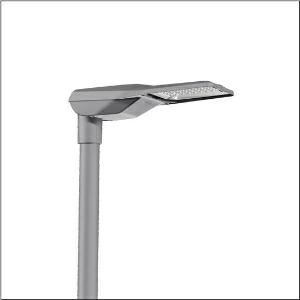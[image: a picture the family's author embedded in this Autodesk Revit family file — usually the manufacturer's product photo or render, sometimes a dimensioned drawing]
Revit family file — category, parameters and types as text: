
# Revit family: streetlight_sl_21_iq_mini___st0_8a_5xe2c31g08gb_0650
name_source: partatom
category: Lighting Fixtures
units: mm (PartAtom-declared; Revit-internal decimal feet)

## family parameters
Cut with Voids When Loaded = No
Host = Face
Light Source = No
Part Type = Normal
Room Calculation Point = No
Round Connector Dimension = Use Diameter
Shared = No

## types (1)
- --- (1 x LED, 5680 lm, 37.1 W, 3000K)
    Apparent Load = 37 VA
    CIE Flux Codes = 38 75 97 100 100
    Color Rendering = 70
    Color Temperature = 3000K
    Default Elevation = 1800 mm
    Description = Streetlight SL 21 iQ mini, mast luminaire, primary light control with lens, of PMMA, primary optical cover: cover, of toughened safety glass, transparent, light distribution: ST0.8a, light emission: direct distribution, primary light characteristic: asymmetric, installation type: post-top, side-entry, LED, High Power LED, rated luminous flux: 5.680lm, luminous efficacy: 153lm/W, light colour: 730, colour temperature: 3000K, control: Street-Remote, Auto-Match, Temp-Guard, Lumen-Switch, Night-Set, Smart-Wire, Light-Fading, Desk-Remote (wireless, voltage-free reading and setting of iQ features in the workshop via application-optimized NFC function/RFID function), optimised constant luminous flux control (CLO 2.0), presetting dimming linear, mains connection: 220..240V, AC, 50/60Hz, start of lifetime: 37W, end of service life: 39W, reduction: 18W, luminaire housing, of diecast aluminium, powder-coated, Siteco® metallic grey (DB 702S), corrosivity category C5 mid according to DIN EN ISO 12944, please order mast flange separately, inclination adjustable: 0°, 5°, 10°, 15°, sealing non-destructively replaceable, multi-level sealing system, length: 628mm, width: 235mm, height: 110mm, mast flange for spigot size: 42mm (side-entry): 5XC10008XM4, 60/48mm (side-entry/post-top): 5XC10108XM2, 76/60mm (side-entry/post-top): 5XC10108XM1, protection rating (complete): IP66, insulation class (complete): insulation class II (safety insulation), certification: CE, ENEC, ENEC+, VDE, impact resistance: IK09, permissible operating ambient temperature for outdoor applications: -40..+50°C, standard-compliant lighting for roads and squares, packaging unit: 1 piece

Light Distribution: ST0.8a
    Height = 110 mm
    Lamp = 1 x LED
    Lamp Light Flux = 5680 lm
    Lamp Power = 37.1 W
    Lamp count = 1
    Length = 625 mm
    Luminous efficacy = 153 lm/W
    Manufacturer = Siteco
    ModVariant = No
    Model = 5XE2C31G08GB
    Number of Poles = 1
    OnlyDefault = Yes
    Power Factor = 1
    Product Name = Streetlight SL 21 iQ mini | ST0.8a
    Product group = mast luminaire | pylon top
    ProductGroupID = 6100
    Protection Class = Protection class II
    Protection Degree = IP 66
    RLX_Detail_Level = 1
    RLX_Emergency_Light_Flux = 0 lm
    RLX_Emergency_Type = 0
    RLX_Emergency_Type_DB = No
    RlxData = <blob elided: 92121 chars, md5=b59b7f38>
    Socket = socket
    Standby Power = 0 W
    System Light Flux = 5680 lm
    System Power = 37 W
    Type Comments = factory setting: luminous flux: 100 % | dim-lin: 254 | 385 mA
    Type Image = l_1003519.jpg
    URL = http://relux.com
    VarID = @adj_118949
    Voltage = 0 V
    Weight = 0.00 kg
    Width = 234 mm

## geometry (parser evidence)
native form markers: Blend x4, Sweep x13
no freeform markers — native parametric forms only
